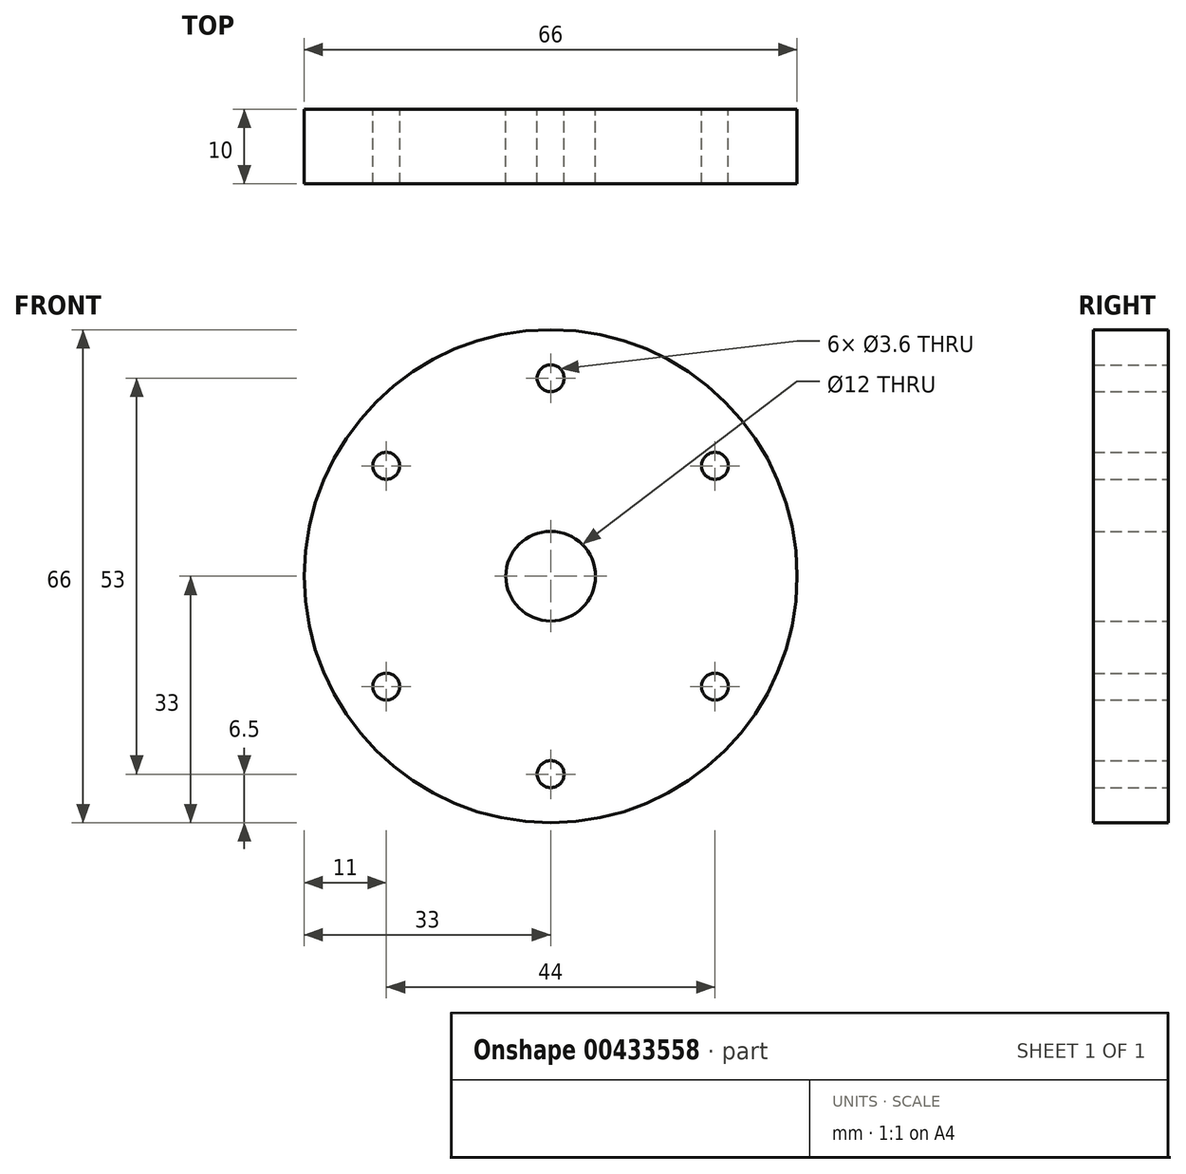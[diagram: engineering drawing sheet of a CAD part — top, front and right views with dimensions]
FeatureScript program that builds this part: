
annotation { "Feature Type Name" : "Feature", "Feature Type Description" : "" }
export const myFeature = defineFeature(function(context is Context, id is Id, definition is map)
    precondition{}
    {
        {
            var Q0;
            Q0=qCreatedBy(makeId("Front.planeOp"),FACE);
            var sketch = newSketch(context, id + "F0", { "sketchPlane" : qUnion([Q0])});
            skCircle(sketch, "E0", {"center": v(0, 0) * mm, "radius": 6 * mm});
            skCircle(sketch, "E1", {"center": v(0, 0) * mm, "radius": 33 * mm});
            skSolve(sketch);
        }
        {
            var Q0;
            Q0 = qSketchRegion(id + "F0", true);
            extrude(context, id + "F1", {"entities" : qUnion([Q0]), "depth" : 10 * mm});
        }
        {
            var Q0;
            Q0=makeQuery(id+"F1.opExtrude","CAP_FACE",FACE,{"disambiguationData":[OSD([sQuery(id+"F0.wireOp",EDGE,"E0"),sQuery(id+"F0.wireOp",EDGE,"E1")])],"isStart":true});
            var sketch = newSketch(context, id + "F2", { "sketchPlane" : qUnion([Q0])});
            skCircle(sketch, "E2", {"center": v(0, 26.5) * mm, "radius": 1.8 * mm});
            skCircle(sketch, "E3", {"center": v(0, -26.5) * mm, "radius": 1.8 * mm});
            skCircle(sketch, "E4", {"center": v(-22, 14.77) * mm, "radius": 1.8 * mm});
            skCircle(sketch, "E5", {"center": v(22, 14.77) * mm, "radius": 1.8 * mm});
            skCircle(sketch, "E6", {"center": v(22, -14.77) * mm, "radius": 1.8 * mm});
            skCircle(sketch, "E7", {"center": v(-22, -14.77) * mm, "radius": 1.8 * mm});
            skSolve(sketch);
        }
        {
            var Q0;
            Q0=makeQuery(id+"F2.imprint","IMPRINT",FACE,{"disambiguationData":[TD([[makeQuery(id+"F2.imprint","IMPRINT",EDGE,{"derivedFrom":sQuery(id+"F2.wireOp",EDGE,"E3")}),1.0]])]});
            var Q1;
            Q1=makeQuery(id+"F2.imprint","IMPRINT",FACE,{"disambiguationData":[TD([[makeQuery(id+"F2.imprint","IMPRINT",EDGE,{"derivedFrom":sQuery(id+"F2.wireOp",EDGE,"E4")}),1.0]])]});
            var Q2;
            Q2=makeQuery(id+"F2.imprint","IMPRINT",FACE,{"disambiguationData":[TD([[makeQuery(id+"F2.imprint","IMPRINT",EDGE,{"derivedFrom":sQuery(id+"F2.wireOp",EDGE,"E5")}),1.0]])]});
            var Q3;
            Q3=makeQuery(id+"F2.imprint","IMPRINT",FACE,{"disambiguationData":[TD([[makeQuery(id+"F2.imprint","IMPRINT",EDGE,{"derivedFrom":sQuery(id+"F2.wireOp",EDGE,"E6")}),1.0]])]});
            var Q4;
            Q4=makeQuery(id+"F2.imprint","IMPRINT",FACE,{"disambiguationData":[TD([[makeQuery(id+"F2.imprint","IMPRINT",EDGE,{"derivedFrom":sQuery(id+"F2.wireOp",EDGE,"E7")}),1.0]])]});
            var Q5;
            Q5=makeQuery(id+"F2.imprint","IMPRINT",FACE,{"disambiguationData":[TD([[makeQuery(id+"F2.imprint","IMPRINT",EDGE,{"derivedFrom":sQuery(id+"F2.wireOp",EDGE,"E2")}),1.0]])]});
            extrude(context, id + "F3", {"entities" : qUnion([Q0, Q1, Q2, Q3, Q4, Q5]), "operationType" : NewBodyOperationType.REMOVE, "oppositeDirection" : true, "depth" : 25 * mm});
        }
    });
